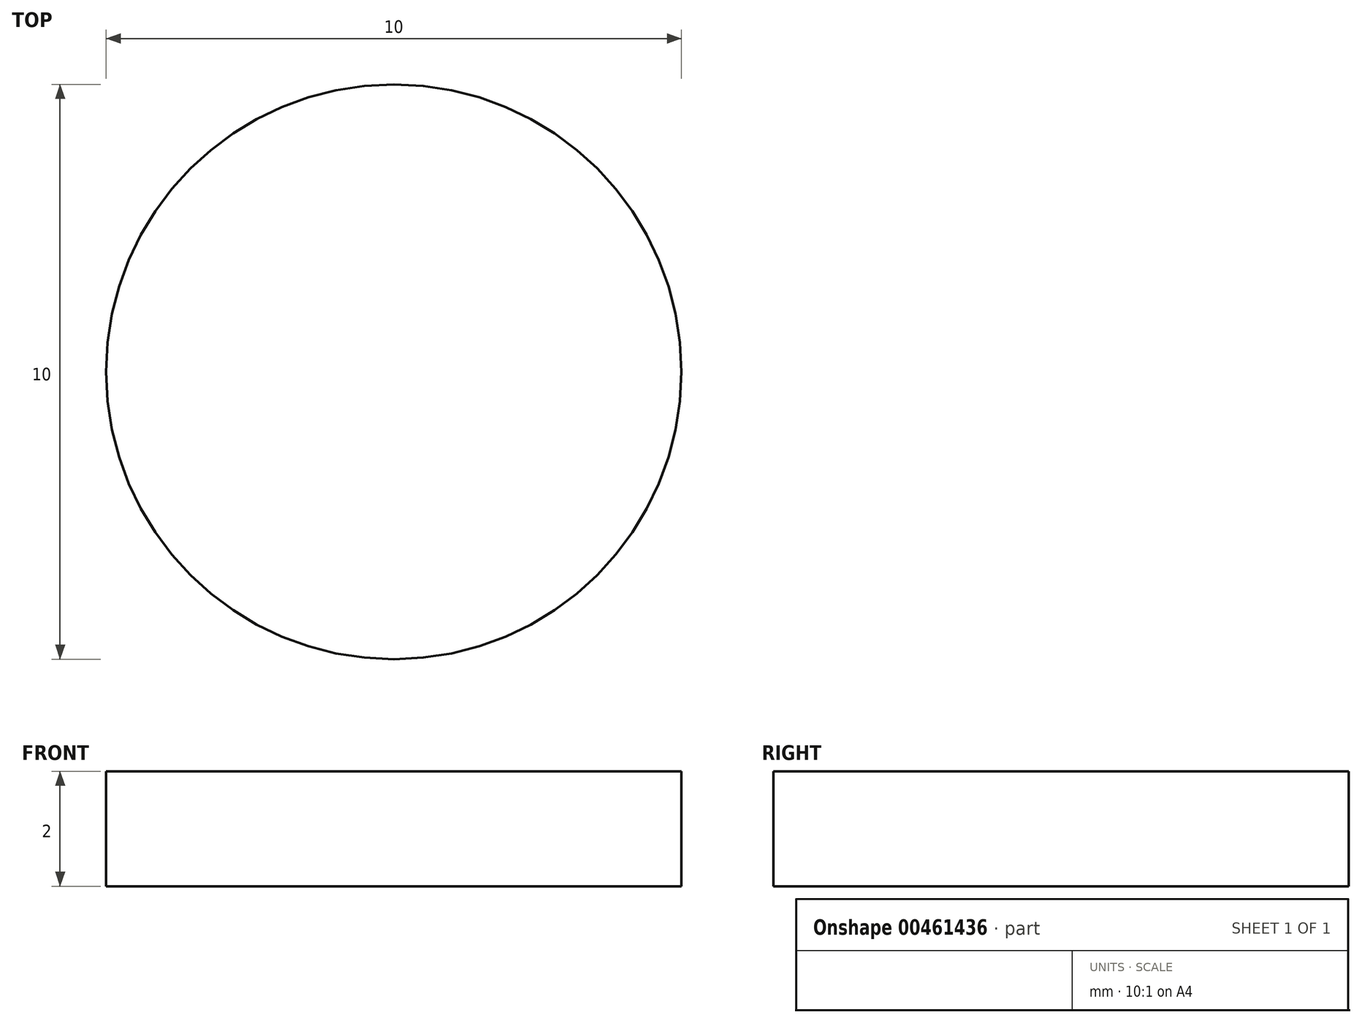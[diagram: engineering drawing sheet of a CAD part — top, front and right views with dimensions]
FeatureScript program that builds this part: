
annotation { "Feature Type Name" : "Feature", "Feature Type Description" : "" }
export const myFeature = defineFeature(function(context is Context, id is Id, definition is map)
    precondition{}
    {
        {
            var Q0;
            Q0=qCreatedBy(makeId("Top.planeOp"),FACE);
            var sketch = newSketch(context, id + "F0", { "sketchPlane" : qUnion([Q0])});
            skCircle(sketch, "E0", {"center": v(0, 0) * mm, "radius": 5 * mm});
            skSolve(sketch);
        }
        {
            var Q0;
            Q0=makeQuery(id+"F0.imprint","IMPRINT",FACE,{"disambiguationData":[TD([[makeQuery(id+"F0.imprint","IMPRINT",EDGE,{"derivedFrom":sQuery(id+"F0.wireOp",EDGE,"E0")}),1.0]])]});
            extrude(context, id + "F1", {"entities" : qUnion([Q0]), "depth" : 2 * mm});
        }
    });
